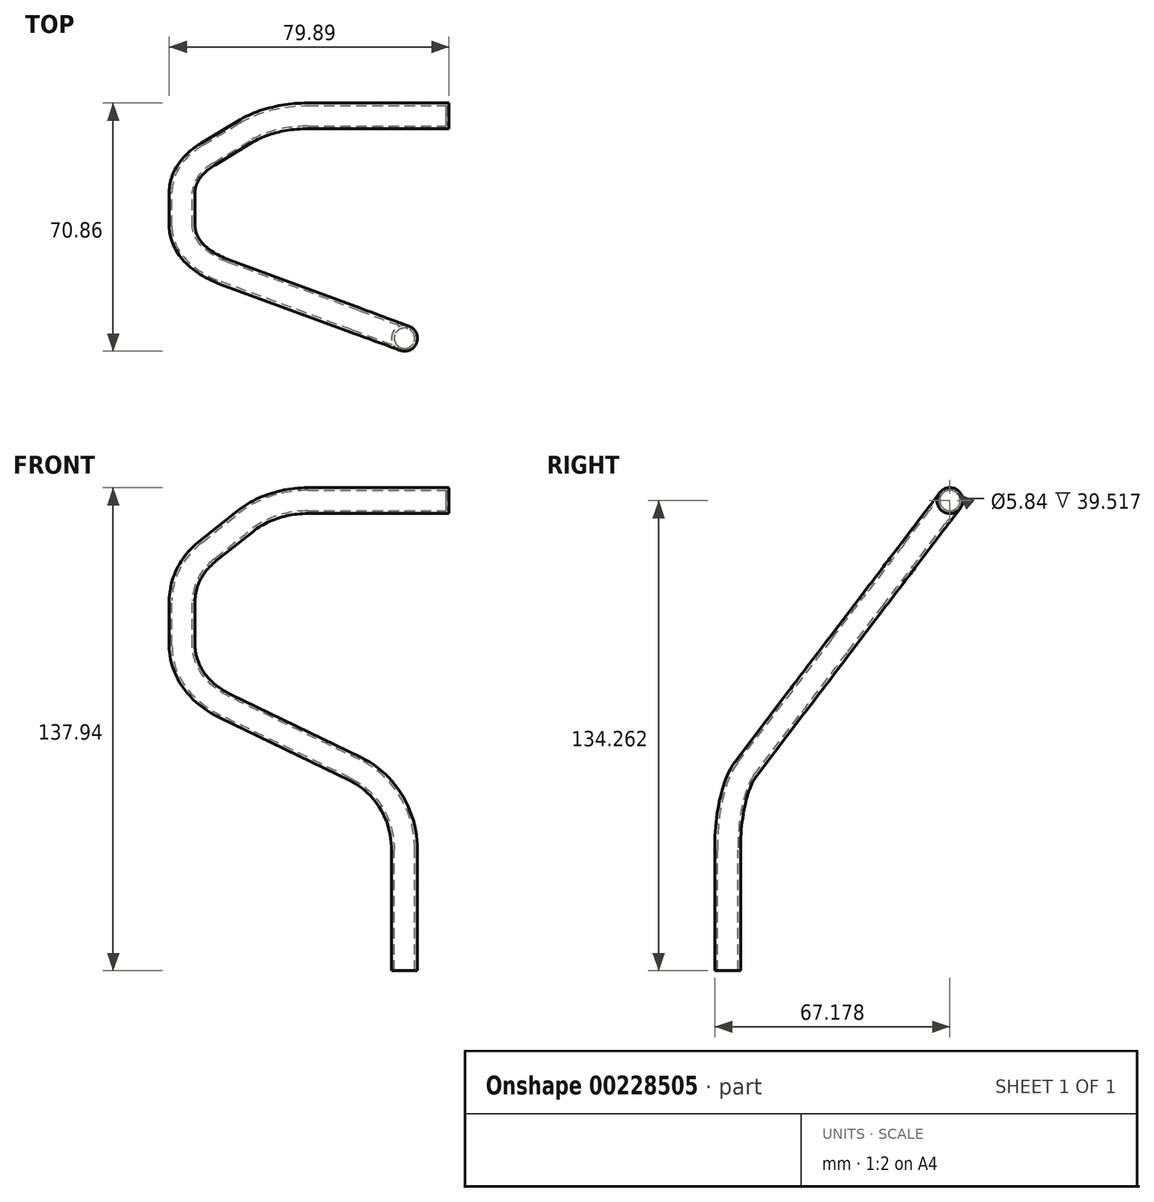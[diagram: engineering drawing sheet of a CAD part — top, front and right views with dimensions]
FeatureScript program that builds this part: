
annotation { "Feature Type Name" : "Feature", "Feature Type Description" : "" }
export const myFeature = defineFeature(function(context is Context, id is Id, definition is map)
    precondition{}
    {
        {
            var Q0;
            Q0=qCreatedBy(makeId("Top.planeOp"),FACE);
            var sketch = newSketch(context, id + "F0", { "sketchPlane" : qUnion([Q0])});
            skLineSegment(sketch, "E0", {"start": v(0, 0) * mm, "end": v(32.86, 0) * mm});
            skLineSegment(sketch, "E1", {"start": v(32.86, 0) * mm, "end": v(32.86, 155.94) * mm});
            skLineSegment(sketch, "E2", {"start": v(0, 0) * mm, "end": v(45.58, 0) * mm});
            skPoint(sketch, "E2.endSnap0", {"position": v(16.43, 0) * mm});
            skLineSegment(sketch, "E3", {"start": v(45.58, 0) * mm, "end": v(45.58, 219.44) * mm});
            skSolve(sketch);
        }
        {
            var Q0;
            Q0=sQuery(id+"F0.wireOp",EDGE,"E1");
            cPlane(context, id + "F1", {"entities" : qUnion([Q0]), "cplaneType" : CPlaneType.LINE_ANGLE, "offset" : 25.4 * mm, "angle" : 90 * degree, "width" : 152.4 * mm, "height" : 152.4 * mm});
        }
        {
            var Q0;
            Q0=qCreatedBy(id+"F1.planeOp",FACE);
            var sketch = newSketch(context, id + "F2", { "sketchPlane" : qUnion([Q0])});
            skLineSegment(sketch, "E4", {"start": v(155.94, 0) * mm, "end": v(155.94, -791.52) * mm});
            skSolve(sketch);
        }
        {
            var Q0;
            Q0=sQuery(id+"F0.wireOp",EDGE,"E3");
            cPlane(context, id + "F3", {"entities" : qUnion([Q0]), "cplaneType" : CPlaneType.LINE_ANGLE, "offset" : 25.4 * mm, "angle" : 90 * degree, "width" : 152.4 * mm, "height" : 152.4 * mm});
        }
        {
            var Q0;
            Q0=qCreatedBy(id+"F3.planeOp",FACE);
            var sketch = newSketch(context, id + "F4", { "sketchPlane" : qUnion([Q0])});
            skLineSegment(sketch, "E5", {"start": v(219.44, 0) * mm, "end": v(219.44, -657.26) * mm});
            skSolve(sketch);
        }
        {
            var Q0;
            Q0=sQuery(id+"F2.wireOp",EDGE,"E4");
            cPlane(context, id + "F5", {"entities" : qUnion([Q0]), "cplaneType" : CPlaneType.LINE_ANGLE, "offset" : 25.4 * mm, "angle" : 0 * degree, "width" : 152.4 * mm, "height" : 152.4 * mm});
        }
        {
            var Q0;
            Q0=qCreatedBy(id+"F5.planeOp",FACE);
            var sketch = newSketch(context, id + "F6", { "sketchPlane" : qUnion([Q0])});
            skLineSegment(sketch, "E6", {"start": v(-155.94, -791.52) * mm, "end": v(-181.34, -791.52) * mm});
            skSolve(sketch);
        }
        {
            var Q0;
            Q0=sQuery(id+"F6.wireOp",EDGE,"E6");
            cPlane(context, id + "F7", {"entities" : qUnion([Q0]), "cplaneType" : CPlaneType.LINE_ANGLE, "offset" : 25.4 * mm, "angle" : 0 * degree, "width" : 152.4 * mm, "height" : 152.4 * mm});
        }
        {
            var Q0;
            Q0=qCreatedBy(id+"F7.planeOp",FACE);
            var sketch = newSketch(context, id + "F8", { "sketchPlane" : qUnion([Q0])});
            skCircle(sketch, "E7", {"center": v(32.86, 155.94) * mm, "radius": 3.68 * mm});
            skSolve(sketch);
        }
        {
            var Q0;
            Q0=sQuery(id+"F4.wireOp",EDGE,"E5");
            cPlane(context, id + "F9", {"entities" : qUnion([Q0]), "cplaneType" : CPlaneType.LINE_ANGLE, "offset" : 25.4 * mm, "angle" : 0 * degree, "width" : 152.4 * mm, "height" : 152.4 * mm});
        }
        {
            var Q0;
            Q0=qCreatedBy(id+"F9.planeOp",FACE);
            var sketch = newSketch(context, id + "F10", { "sketchPlane" : qUnion([Q0])});
            skCircle(sketch, "E8", {"center": v(-219.44, -657.26) * mm, "radius": 3.68 * mm});
            skSolve(sketch);
        }
        {
            var Q0;
            Q0=sQuery(id+"F4.wireOp",EDGE,"E5");
            cPlane(context, id + "F11", {"entities" : qUnion([Q0]), "cplaneType" : CPlaneType.LINE_ANGLE, "offset" : 25.4 * mm, "angle" : 90 * degree, "width" : 152.4 * mm, "height" : 152.4 * mm});
        }
        {
            var Q0;
            Q0=qCreatedBy(id+"F11.planeOp",FACE);
            var sketch = newSketch(context, id + "F12", { "sketchPlane" : qUnion([Q0])});
            skLineSegment(sketch, "E9", {"start": v(-45.58, -657.26) * mm, "end": v(5.22, -657.26) * mm});
            skSolve(sketch);
        }
        {
            var Q0;
            Q0=qCreatedBy(id+"F5.planeOp",FACE);
            var sketch = newSketch(context, id + "F13", { "sketchPlane" : qUnion([Q0])});
            skLineSegment(sketch, "E10", {"start": v(-155.94, -791.52) * mm, "end": v(-155.94, -740.72) * mm});
            skSolve(sketch);
        }
        {
            var Q0;
            Q0=sQuery(id+"F13.wireOp",VERTEX,"E10.end");
            var Q1;
            Q1=sQuery(id+"F12.wireOp",VERTEX,"E9.start");
            var Q2;
            Q2=sQuery(id+"F12.wireOp",VERTEX,"E9.end");
            cPlane(context, id + "F14", {"entities" : qUnion([Q0, Q1, Q2]), "cplaneType" : CPlaneType.THREE_POINT, "offset" : 25.4 * mm, "width" : 152.4 * mm, "height" : 152.4 * mm});
        }
        {
            var Q0;
            Q0=qCreatedBy(id+"F14.planeOp",FACE);
            var sketch = newSketch(context, id + "F15", { "sketchPlane" : qUnion([Q0])});
            skLineSegment(sketch, "E11", {"start": v(12.66, -397.65) * mm, "end": v(23.19, -408.17) * mm});
            skLineSegment(sketch, "E12", {"start": v(18.42, -463.88) * mm, "end": v(-32.86, -495.08) * mm});
            skLineSegment(sketch, "E13", {"start": v(30.62, -426.13) * mm, "end": v(30.62, -442.18) * mm});
            skPoint(sketch, "E13.endSnap0", {"position": v(30.62, -441) * mm});
            skPoint(sketch, "E14.orphan", {"position": v(56.02, -441) * mm});
            skLineSegment(sketch, "E15", {"start": v(-5.3, -390.2) * mm, "end": v(-45.58, -390.2) * mm});
            skPoint(sketch, "E16.end.orphan", {"position": v(5.22, -441) * mm});
            skPoint(sketch, "E17.visualSharp", {"position": v(5.22, -390.2) * mm});
            skArc(sketch, "E17.filletArc", {"start": v(12.66, -397.65) * mm, "mid": v(4.42, -392.14) * mm, "end": v(-5.3, -390.2) * mm});
            skPoint(sketch, "E18.visualSharp", {"position": v(30.62, -415.6) * mm});
            skArc(sketch, "E18.filletArc", {"start": v(30.62, -426.13) * mm, "mid": v(28.7, -416.4) * mm, "end": v(23.19, -408.17) * mm});
            skPoint(sketch, "E19.visualSharp", {"position": v(30.62, -456.46) * mm});
            skArc(sketch, "E19.filletArc", {"start": v(18.42, -463.88) * mm, "mid": v(27.37, -454.63) * mm, "end": v(30.62, -442.18) * mm});
            skSolve(sketch);
        }
        {
            var Q0;
            Q0=sQuery(id+"F15.wireOp",EDGE,"E12");
            var Q1;
            Q1=sQuery(id+"F13.wireOp",EDGE,"E10");
            cPlane(context, id + "F16", {"entities" : qUnion([Q0, Q1]), "cplaneType" : CPlaneType.LINE_ANGLE, "offset" : 25.4 * mm, "angle" : 0 * degree, "width" : 152.4 * mm, "height" : 152.4 * mm});
        }
        {
            var Q0;
            Q0=qCreatedBy(id+"F16.planeOp",FACE);
            var sketch = newSketch(context, id + "F17", { "sketchPlane" : qUnion([Q0])});
            skLineSegment(sketch, "E20", {"start": v(-23.06, -791.52) * mm, "end": v(-23.06, -757.08) * mm});
            skLineSegment(sketch, "E21", {"start": v(-37.95, -733.95) * mm, "end": v(-77.71, -715.89) * mm});
            skPoint(sketch, "E22.visualSharp", {"position": v(-23.06, -740.72) * mm});
            skArc(sketch, "E22.filletArc", {"start": v(-23.06, -757.08) * mm, "mid": v(-27.1, -743.32) * mm, "end": v(-37.95, -733.95) * mm});
            skSolve(sketch);
        }
        {
            var Q0;
            Q0=makeQuery(id+"F8.imprint","IMPRINT",FACE,{"disambiguationData":[TD([[makeQuery(id+"F8.imprint","IMPRINT",EDGE,{"derivedFrom":sQuery(id+"F8.wireOp",EDGE,"E7")}),1.0]])]});
            var Q1;
            Q1=sQuery(id+"F17.wireOp",EDGE,"E20");
            var Q2;
            Q2=sQuery(id+"F17.wireOp",EDGE,"E22.filletArc");
            var Q3;
            Q3=sQuery(id+"F17.wireOp",EDGE,"E21");
            var Q4;
            Q4=sQuery(id+"F15.wireOp",EDGE,"E19.filletArc");
            var Q5;
            Q5=sQuery(id+"F15.wireOp",EDGE,"E13");
            var Q6;
            Q6=sQuery(id+"F15.wireOp",EDGE,"E18.filletArc");
            var Q7;
            Q7=sQuery(id+"F15.wireOp",EDGE,"E11");
            var Q8;
            Q8=sQuery(id+"F15.wireOp",EDGE,"E17.filletArc");
            var Q9;
            Q9=sQuery(id+"F15.wireOp",EDGE,"E15");
            sweep(context, id + "F18", {"profiles" : qUnion([Q0]), "path" : qUnion([Q1, Q2, Q3, Q4, Q5, Q6, Q7, Q8, Q9])});
        }
        {
            var Q0;
            Q0=makeQuery(id+"F18.opSweep","CAP_FACE",FACE,{"disambiguationData":[OSD([sQuery(id+"F8.wireOp",EDGE,"E7"),sQuery(id+"F17.wireOp",VERTEX,"E20.start")])],"isStart":true});
            shell(context, id + "F19", {"entities" : qUnion([Q0]), "thickness" : 0.76 * mm});
        }
    });
